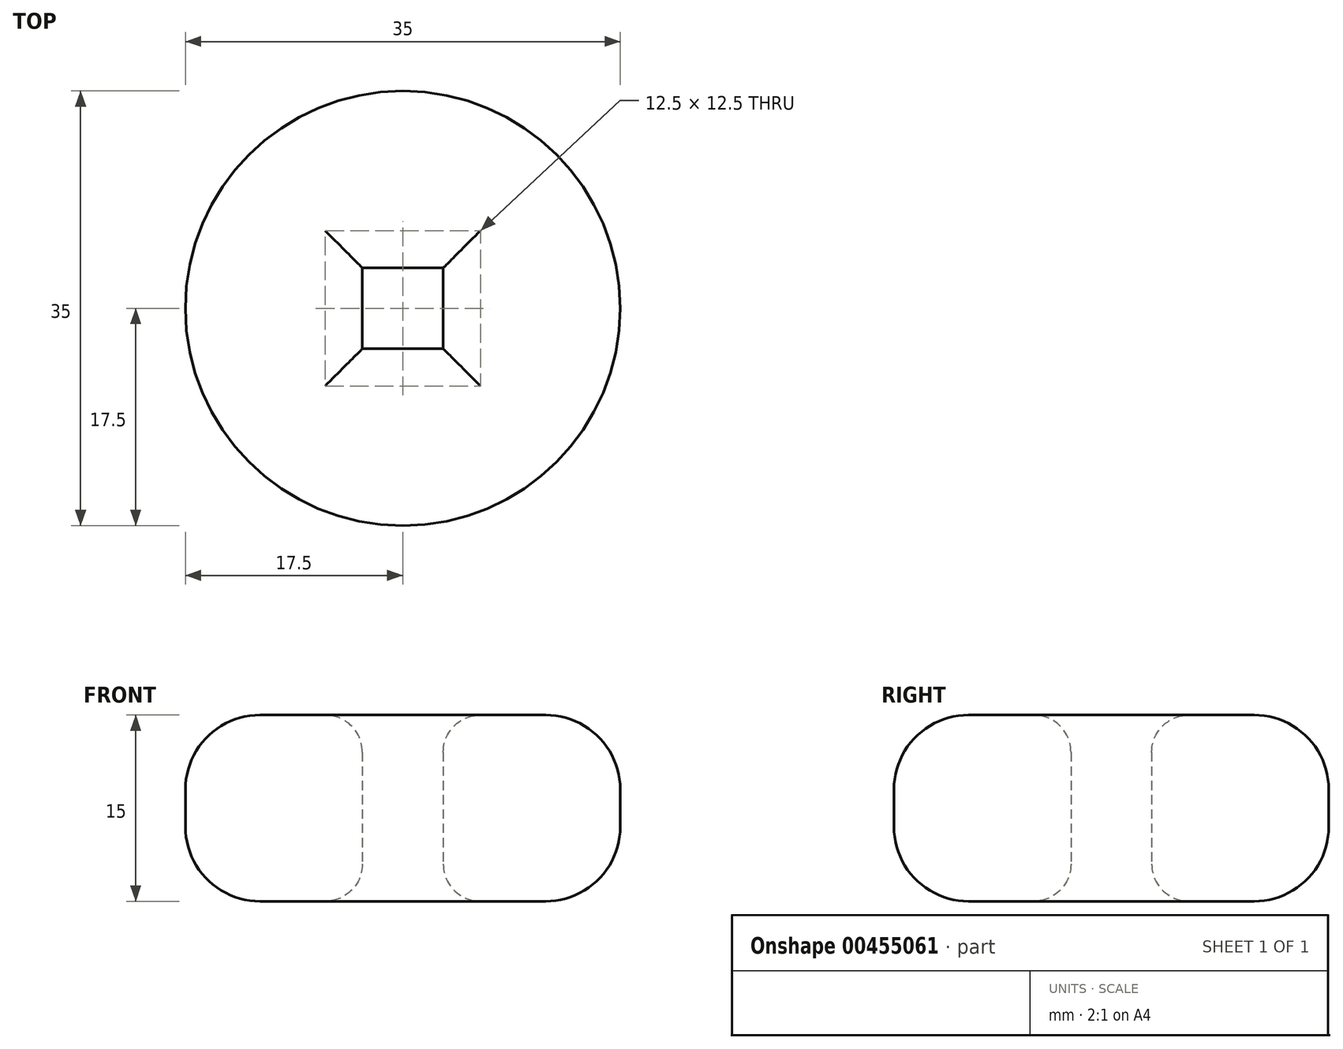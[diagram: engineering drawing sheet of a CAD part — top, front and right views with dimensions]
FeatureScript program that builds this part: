
annotation { "Feature Type Name" : "Feature", "Feature Type Description" : "" }
export const myFeature = defineFeature(function(context is Context, id is Id, definition is map)
    precondition{}
    {
        {
            var Q0;
            Q0=qCreatedBy(makeId("Top.planeOp"),FACE);
            var sketch = newSketch(context, id + "F0", { "sketchPlane" : qUnion([Q0])});
            skCircle(sketch, "E0", {"center": v(0, 0) * mm, "radius": 17.5 * mm});
            skLineSegment(sketch, "E1.bottom", {"start": v(3.25, -3.25) * mm, "end": v(-3.25, -3.25) * mm});
            skLineSegment(sketch, "E1.top", {"start": v(3.25, 3.25) * mm, "end": v(-3.25, 3.25) * mm});
            skLineSegment(sketch, "E1.left", {"start": v(3.25, -3.25) * mm, "end": v(3.25, 3.25) * mm});
            skLineSegment(sketch, "E1.right", {"start": v(-3.25, -3.25) * mm, "end": v(-3.25, 3.25) * mm});
            skSolve(sketch);
        }
        {
            var Q0;
            Q0=makeQuery(id+"F0.imprint","IMPRINT",FACE,{"disambiguationData":[TD([[makeQuery(id+"F0.imprint","IMPRINT",EDGE,{"derivedFrom":sQuery(id+"F0.wireOp",EDGE,"E0")}),1.0]])]});
            extrude(context, id + "F1", {"entities" : qUnion([Q0]), "depth" : 15 * mm});
        }
        {
            var Q0;
            Q0=makeQuery(id+"F1.opExtrude","CAP_EDGE",EDGE,{"disambiguationData":[OSD([sQuery(id+"F0.wireOp",EDGE,"E0")])],"isStart":false});
            var Q1;
            Q1=makeQuery(id+"F1.opExtrude","CAP_EDGE",EDGE,{"disambiguationData":[OSD([sQuery(id+"F0.wireOp",EDGE,"E0")])],"isStart":true});
            fillet(context, id + "F2", {"entities" : qUnion([Q0, Q1]), "radius" : 6 * mm, "tangentPropagation" : true, "allowEdgeOverflow" : false});
        }
        {
            var Q0;
            Q0=makeQuery(id+"F1.opExtrude","CAP_EDGE",EDGE,{"disambiguationData":[OSD([sQuery(id+"F0.wireOp",EDGE,"aFgaoz9V-Ca7q-axmY-a975-9k1QYWRIUf0o")])],"isStart":false});
            var Q1;
            Q1=makeQuery(id+"F1.opExtrude","CAP_EDGE",EDGE,{"disambiguationData":[OSD([sQuery(id+"F0.wireOp",EDGE,"aFgaoz9V-Ca7q-axmY-a975-9k1QYWRIUf0o")])],"isStart":true});
            var Q2;
            Q2=makeQuery(id+"F1.opExtrude","CAP_EDGE",EDGE,{"disambiguationData":[OSD([sQuery(id+"F0.wireOp",EDGE,"E1.right")])],"isStart":false});
            var Q3;
            Q3=makeQuery(id+"F1.opExtrude","CAP_EDGE",EDGE,{"disambiguationData":[OSD([sQuery(id+"F0.wireOp",EDGE,"E1.top")])],"isStart":false});
            var Q4;
            Q4=makeQuery(id+"F1.opExtrude","CAP_EDGE",EDGE,{"disambiguationData":[OSD([sQuery(id+"F0.wireOp",EDGE,"E1.left")])],"isStart":false});
            var Q5;
            Q5=makeQuery(id+"F1.opExtrude","CAP_EDGE",EDGE,{"disambiguationData":[OSD([sQuery(id+"F0.wireOp",EDGE,"E1.bottom")])],"isStart":false});
            var Q6;
            Q6=makeQuery(id+"F1.opExtrude","CAP_EDGE",EDGE,{"disambiguationData":[OSD([sQuery(id+"F0.wireOp",EDGE,"E1.top")])],"isStart":true});
            var Q7;
            Q7=makeQuery(id+"F1.opExtrude","CAP_EDGE",EDGE,{"disambiguationData":[OSD([sQuery(id+"F0.wireOp",EDGE,"E1.right")])],"isStart":true});
            var Q8;
            Q8=makeQuery(id+"F1.opExtrude","CAP_EDGE",EDGE,{"disambiguationData":[OSD([sQuery(id+"F0.wireOp",EDGE,"E1.bottom")])],"isStart":true});
            var Q9;
            Q9=makeQuery(id+"F1.opExtrude","CAP_EDGE",EDGE,{"disambiguationData":[OSD([sQuery(id+"F0.wireOp",EDGE,"E1.left")])],"isStart":true});
            fillet(context, id + "F3", {"entities" : qUnion([Q0, Q1, Q2, Q3, Q4, Q5, Q6, Q7, Q8, Q9]), "radius" : 3 * mm, "tangentPropagation" : true, "allowEdgeOverflow" : false});
        }
    });
